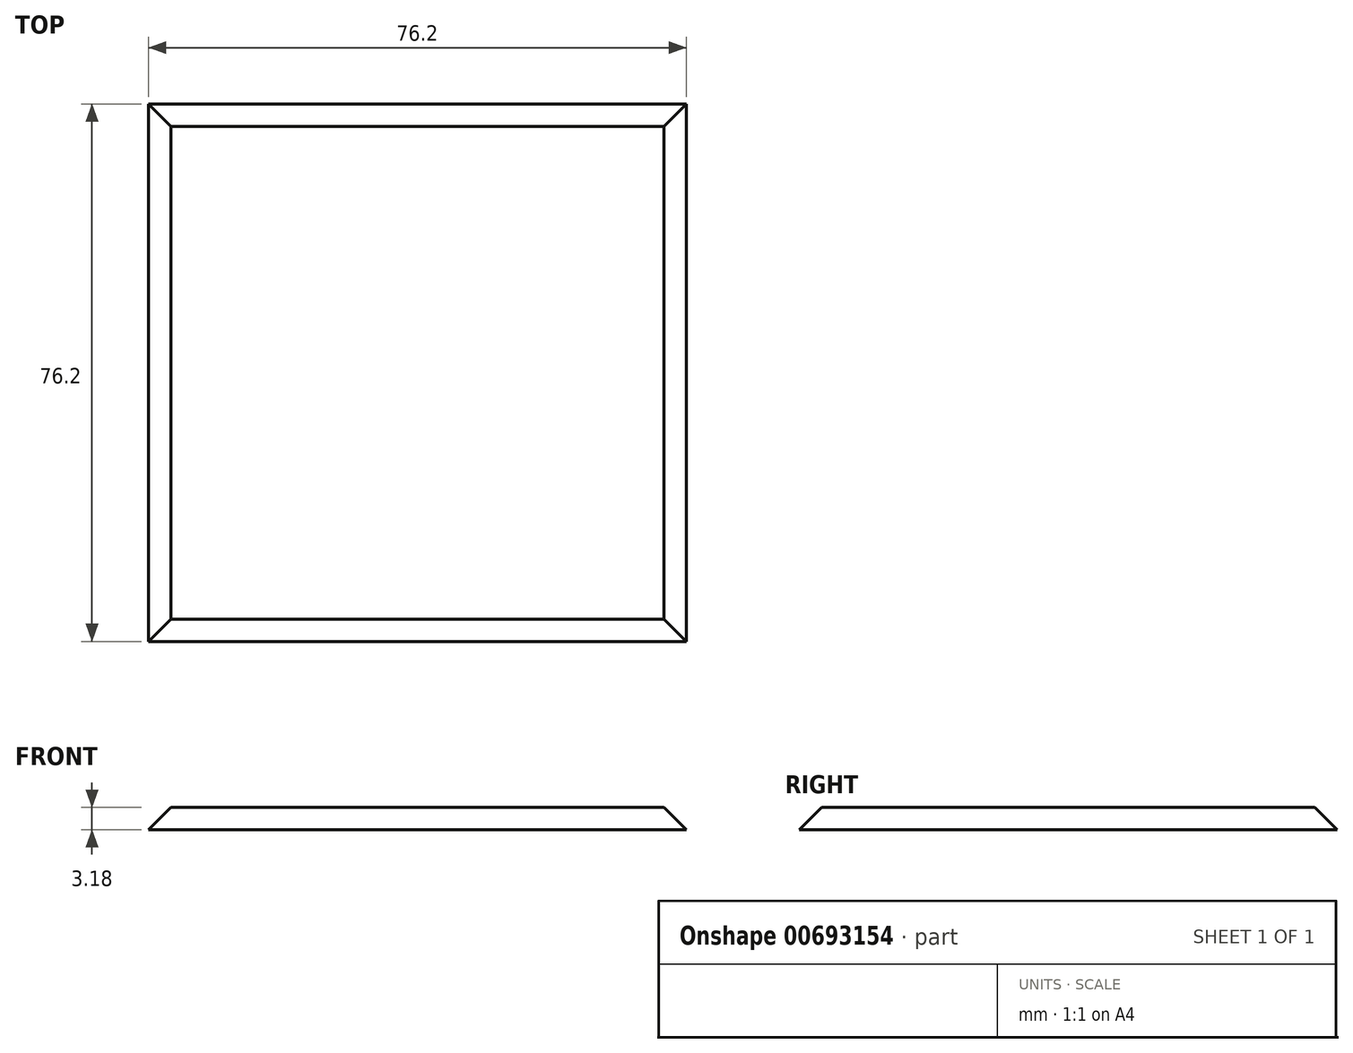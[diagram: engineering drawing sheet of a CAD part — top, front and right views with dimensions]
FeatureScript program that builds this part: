
annotation { "Feature Type Name" : "Feature", "Feature Type Description" : "" }
export const myFeature = defineFeature(function(context is Context, id is Id, definition is map)
    precondition{}
    {
        {
            var Q0;
            Q0=qCreatedBy(makeId("Top.planeOp"),FACE);
            var sketch = newSketch(context, id + "F0", { "sketchPlane" : qUnion([Q0])});
            skLineSegment(sketch, "E0.bottom", {"start": v(38.1, 38.1) * mm, "end": v(-38.1, 38.1) * mm});
            skLineSegment(sketch, "E0.top", {"start": v(38.1, -38.1) * mm, "end": v(-38.1, -38.1) * mm});
            skLineSegment(sketch, "E0.left", {"start": v(38.1, 38.1) * mm, "end": v(38.1, -38.1) * mm});
            skLineSegment(sketch, "E0.right", {"start": v(-38.1, 38.1) * mm, "end": v(-38.1, -38.1) * mm});
            skPoint(sketch, "E0.middle", {"position": v(0, 0) * mm});
            skSolve(sketch);
        }
        {
            var Q0;
            Q0 = qSketchRegion(id + "F0", true);
            extrude(context, id + "F1", {"entities" : qUnion([Q0]), "depth" : 3.17 * mm, "offsetDistance" : 25.4 * mm});
        }
        {
            var Q0;
            Q0=makeQuery(id+"F1.opExtrude","SWEPT_FACE",FACE,{"disambiguationData":[OSD([sQuery(id+"F0.wireOp",EDGE,"E0.left")])]});
            var sketch = newSketch(context, id + "F2", { "sketchPlane" : qUnion([Q0])});
            skLineSegment(sketch, "E1", {"start": v(-38.1, 0) * mm, "end": v(-34.93, 3.17) * mm});
            skLineSegment(sketch, "E2", {"start": v(-34.93, 3.17) * mm, "end": v(-38.1, 3.18) * mm});
            skLineSegment(sketch, "E3", {"start": v(-38.1, 3.18) * mm, "end": v(-38.1, 0) * mm});
            skLineSegment(sketch, "E4", {"start": v(0, 12.24) * mm, "end": v(0, -11.06) * mm, "construction": true});
            skLineSegment(sketch, "E5.MirrorCS", {"start": v(38.1, 0) * mm, "end": v(34.93, 3.17) * mm});
            skLineSegment(sketch, "E6.MirrorCS", {"start": v(34.93, 3.17) * mm, "end": v(38.1, 3.18) * mm});
            skLineSegment(sketch, "E7.MirrorCS", {"start": v(38.1, 3.18) * mm, "end": v(38.1, 0) * mm});
            skSolve(sketch);
        }
        {
            var Q0;
            Q0=makeQuery(id+"F1.opExtrude","SWEPT_FACE",FACE,{"disambiguationData":[OSD([sQuery(id+"F0.wireOp",EDGE,"E0.bottom")])]});
            var sketch = newSketch(context, id + "F3", { "sketchPlane" : qUnion([Q0])});
            skLineSegment(sketch, "E8", {"start": v(-38.1, 0) * mm, "end": v(-34.93, 3.17) * mm});
            skLineSegment(sketch, "E9", {"start": v(-34.93, 3.18) * mm, "end": v(-38.1, 3.18) * mm});
            skLineSegment(sketch, "E10", {"start": v(-38.1, 3.18) * mm, "end": v(-38.1, 0) * mm});
            skLineSegment(sketch, "E11", {"start": v(0, 8.91) * mm, "end": v(0, -4.58) * mm, "construction": true});
            skLineSegment(sketch, "E12.MirrorCS", {"start": v(38.1, 0) * mm, "end": v(34.93, 3.17) * mm});
            skLineSegment(sketch, "E13.MirrorCS", {"start": v(34.93, 3.18) * mm, "end": v(38.1, 3.18) * mm});
            skLineSegment(sketch, "E14.MirrorCS", {"start": v(38.1, 3.18) * mm, "end": v(38.1, 0) * mm});
            skSolve(sketch);
        }
        {
            var Q0;
            Q0=makeQuery(id+"F3.imprint","IMPRINT",FACE,{"disambiguationData":[TD([[makeQuery(id+"F3.imprint","IMPRINT",EDGE,{"derivedFrom":sQuery(id+"F3.wireOp",EDGE,"E8")}),1.0]])]});
            var Q1;
            Q1=makeQuery(id+"F3.imprint","IMPRINT",FACE,{"disambiguationData":[TD([[makeQuery(id+"F3.imprint","IMPRINT",EDGE,{"derivedFrom":sQuery(id+"F3.wireOp",EDGE,"E12.MirrorCS")}),-1.0]])]});
            extrude(context, id + "F4", {"entities" : qUnion([Q0, Q1]), "operationType" : NewBodyOperationType.REMOVE, "oppositeDirection" : true, "depth" : 76.2 * mm, "offsetDistance" : 25.4 * mm});
        }
        {
            var Q0;
            Q0=makeQuery(id+"F2.imprint","IMPRINT",FACE,{"disambiguationData":[TD([[makeQuery(id+"F2.imprint","IMPRINT",EDGE,{"derivedFrom":sQuery(id+"F2.wireOp",EDGE,"E5.MirrorCS")}),-1.0]])]});
            var Q1;
            Q1=makeQuery(id+"F2.imprint","IMPRINT",FACE,{"disambiguationData":[TD([[makeQuery(id+"F2.imprint","IMPRINT",EDGE,{"derivedFrom":sQuery(id+"F2.wireOp",EDGE,"E1")}),1.0]])]});
            extrude(context, id + "F5", {"entities" : qUnion([Q0, Q1]), "operationType" : NewBodyOperationType.REMOVE, "oppositeDirection" : true, "depth" : 76.2 * mm, "offsetDistance" : 25.4 * mm});
        }
    });
